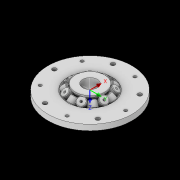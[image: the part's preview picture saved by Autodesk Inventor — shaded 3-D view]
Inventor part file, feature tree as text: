
AUTODESK INVENTOR PART (.ipt)
format: ipt  version: 2022.2 (Build 262287010, 287A)  size: 992,256 bytes
history: native  units: mm
features: other x35, extrude x26, sketch x16, pattern_circular x10, plane x4, fillet x2, move_body x2, revolve x2, draft x2, chamfer x2
ambient origin geometry x8: Origin, YZ Plane, XZ Plane, XY Plane, X Axis, Y Axis, Z Axis, Center Point
bodies: Solid5 (feature_tree)
feature tree (101):
  other  "CrossSection1"
  sketch  "Sketch7"  dims[d167=8.972256mm]
  other  "Roller1"
  other  "Roller2"
  sketch  "Sketch22"  dims[d173=10.814812mm d201=40.0mm]
  sketch  "Sketch2"  dims[d57=4.025mm d90=18.336628mm]
  sketch  "Sketch23"  dims[d232=0.0mm d233=3600.0mm d343=17.202946mm d344=17.117234mm]
  other  "RevRoller1"
  fillet  "Fillet1"  Radius=15.781563mm
  extrude  "Extrusion39"  Depth=18.336628mm
  pattern_circular  "Circular Pattern13"  Count=4  [1 undecoded]
  move_body  "Move Body7"
  revolve  "Revolution13"  [1 undecoded]
  fillet  "Fillet3"  Radius=17.117234mm
  pattern_circular  "Circular Pattern14"  [2 undecoded]
  move_body  "Move Body6"
  revolve  "Revolution14"  [1 undecoded]
  other  "OuterRim_Top2"
  other  "OuterRim_Bottom2"
  plane  "Work Plane8"
  sketch  "Sketch49"  dims[d352=0.025mm]
  sketch  "Sketch50"  dims[d354=0.025mm]
  sketch  "Sketch51"  dims[d355=17.202946mm]
  extrude  "Extrusion40"  TaperAngle=360.0deg  [1 undecoded]
  extrude  "Extrusion41"  Depth=0.5mm
  extrude  "Extrusion42"  Depth=0.5mm
  extrude  "Extrusion43"  Depth=0.5mm
  sketch  "Sketch52"  dims[d356=17.117234mm]
  extrude  "Extrusion44"  Depth=0.5mm
  extrude  "Extrusion45"  Depth=0.5mm
  extrude  "Extrusion46"  TaperAngle=90.0deg  [1 undecoded]
  extrude  "Extrusion47"  Depth=0.5mm
  pattern_circular  "Circular Pattern32"  Count=7  [1 undecoded]
  pattern_circular  "Circular Pattern33"  Angle=360.0deg  [1 undecoded]
  sketch  "Sketch57"  dims[d358=360.0deg d359=0.5mm d360=70.0mm d361=360.0deg d363=4.48799mm d367=8.1mm d370=0.025mm d371=1.0mm d372=4.48799mm d373=90.0deg d374=0.5mm d375=70.0mm d376=360.0deg d378=90.0deg d379=0.1mm d380=0.025mm d381=0.025mm d382=0.025mm d383=0.025mm d384=10.620203mm d385=0.0mm d386=0.0mm d391=7.0mm d392=40.0mm d393=1.5mm d394=1.5mm d395=1.5mm d396=1.5mm d397=90.0deg d398=90.0deg d399=90.0deg d400=40.0mm d401=10.620203mm d402=0.0mm d486=0.436332mm d487=0.5mm d488=2.0mm d489=0.0mm d490=20.0mm d495=2.5mm d496=8.0mm d506=13.856406mm d507=55.5mm d508=8.0mm d509=0.05mm d510=2.5mm d511=30.0deg d512=12.0mm d513=6.0mm d514=0.2mm d515=30.0deg d516=131.0mm d517=65.5mm d518=0.2mm d519=100.0mm d520=120.0mm d521=2.0mm d522=150.0mm d530=50.0mm d531=5.5mm d532=5.5mm d533=5.5mm d534=85.75mm d535=73.5mm d536=61.25mm d537=24.5mm d538=3.0mm d539=2.4mm d540=0.0mm d541=0.0mm d542=0.0mm d543=5.5mm d544=3.0mm d545=0.0mm d546=90.0mm d547=360.0deg d549=3.0mm d550=3.0mm d551=2.4mm d552=0.0mm d553=5.310101mm d554=0.0mm d555=2.4mm d556=0.0mm d557=5.310101mm d558=0.0mm d559=5.310101mm d560=0.0mm d561=90.0mm d562=360.0deg d564=60.0mm d565=360.0deg d567=5.5mm d568=5.5mm d569=3.0mm d570=0.0mm d571=5.310101mm d572=0.0mm d573=3.0mm d574=0.0mm d575=5.310101mm d576=0.0mm d577=90.0mm d578=360.0deg d580=60.0mm d581=360.0deg d584=20.0mm d585=8.0mm d587=1.75mm d589=3.0mm d592=2.0mm d593=12.0mm d594=12.0mm d600=0.5mm d601=2.0mm d602=45.0deg d603=0.5mm d604=2.0mm d605=45.0deg d606=0.436332mm d607=0.5mm d608=0.0mm d609=20.0mm d611=360.0deg d613=0.0mm d614=0.0mm d617=0.99971mm d618=100.0mm d620=34.0mm d621=5.0mm d622=0.5mm d623=0.5mm d624=5.0mm d625=0.2mm d626=0.0mm d627=20.0mm d629=34.0mm d630=48.5mm d631=20.0mm d633=6.283185mm d635=5.5mm d636=3.0mm d637=7.0mm d638=4.0mm d639=5.310101mm d640=0.0mm d641=3.0mm d642=0.0mm d643=5.310101mm d644=0.0mm d645=4.0mm d646=0.0mm d647=20.0mm d649=6.283185mm d651=3.0mm d652=4.0mm d653=20.0mm d655=6.283185mm d657=7.0mm d658=5.5mm d659=5.310101mm d660=0.0mm d661=2.020203mm d662=0.0mm d663=5.310101mm d664=0.0mm d665=2.620203mm d666=0.0mm d679=50.0mm d680=360.0deg d682=50.0mm d683=360.0deg d694=6.35mm d695=6.35mm d696=6.4mm d697=5.45mm d698=11.194mm d699=0.0mm d700=8.194mm d701=0.0mm d702=60.0mm d703=360.0deg d705=0.0mm d706=0.0mm d707=0.0mm d708=0.0mm d709=0.0mm d710=0.0mm d711=0.0mm d712=0.0mm d713=0.0mm d714=0.0mm d715=0.0mm d716=0.0mm d16=0.872665mm d17=0.872665mm d49=0.872665mm d50=0.872665mm d51=0.872665mm d52=0.872665mm d236=0.5mm d237=0.872665mm d238=0.5mm d239=0.872665mm d282=1.0mm d283=1.0mm d284=1.0mm d285=0.15mm d286=0.25mm d287=0.375mm d288=14.3117mm d289=0.75mm d290=20.594885mm d291=0.0625mm d292=0.75mm d293=0.375mm d405=0.5mm d406=0.872665mm d407=0.5mm d408=0.872665mm d413=0.5mm d414=0.872665mm d415=0.5mm d416=0.872665mm d417=0.5mm d418=0.872665mm d419=0.5mm d420=0.872665mm d421=0.872665mm d431=0.5mm d432=0.872665mm d433=0.5mm d434=0.872665mm d471=0.5mm d472=0.872665mm d473=0.5mm d474=0.872665mm d497=0.5mm d498=0.872665mm d499=0.5mm d500=0.872665mm d590=0.5mm d591=0.872665mm]
  other  "UCS2"
  extrude  "Extrusion50"  TaperAngle=90.0deg  [1 undecoded]
  extrude  "Extrusion51"  Depth=0.1mm
  pattern_circular  "Circular Pattern34"  [2 undecoded]
  other  "UCS1"
  plane  "Work Plane7"
  sketch  "Sketch47"  dims[d350=17.202946mm]
  extrude  "Rotor_Ring"  Depth=0.5mm
  draft  "FaceDraft2"
  sketch  "Sketch30"  dims[d345=0.025mm]
  plane  "Work Plane5"
  other  "Rotor Featurs"
  other  "RotorRim_Bottom"
  extrude  "Extrusion24"  Depth=0.5mm
  extrude  "Extrusion25"  Depth=0.5mm
  extrude  "Extrusion26"  Depth=10.620203mm
  pattern_circular  "Circular Pattern23"  [2 undecoded]
  sketch  "Sketch41"  dims[d347=0.1mm]
  extrude  "Extrusion27"  TaperAngle=0.0deg  [1 undecoded]
  extrude  "Extrusion28"  Depth=7.0mm
  pattern_circular  "Circular Pattern24"  Count=4  [1 undecoded]
  extrude  "Extrusion29"  Depth=0.5mm
  extrude  "Extrusion30"  Depth=0.5mm
  extrude  "Extrusion31"  Depth=0.5mm
  pattern_circular  "Circular Pattern25"  [2 undecoded]
  sketch  "Sketch42"  dims[d348=0.1mm]
  extrude  "Extrusion32"  TaperAngle=90.0deg  [1 undecoded]
  extrude  "Extrusion33"  TaperAngle=90.0deg  [1 undecoded]
  extrude  "Extrusion34"  TaperAngle=90.0deg  [1 undecoded]
  extrude  "Extrusion35"  Depth=40.0mm
  pattern_circular  "Circular Pattern26"  [2 undecoded]
  pattern_circular  "Circular Pattern27"  [2 undecoded]
  chamfer  "Chamfer1"  Distance=0.436332mm
  chamfer  "Chamfer2"  Distance=0.5mm
  draft  "FaceDraft4"
  plane  "Work Plane6"
  sketch  "Sketch43"  dims[d349=17.117234mm]
  extrude  "Extrusion37"  Depth=0.5mm
  extrude  "Extrusion38"  Depth=8.0mm
  other  "2D Equation Curve1"
  sketch  "Sketch40"  dims[d346=0.025mm]
  other  "Work Axis6"
  other  "Work Axis7"
  other  "Work Axis8"
  other  "Work Axis9"
  other  "Work Axis10"
  other  "Work Point1"
  other  "Work Point2"
  other  "Work Point3"
  other  "Work Point4"
  other  "Work Point5"
  sketch  "Sketch48"  dims[d351=0.025mm]
  other  "UCS1: YZ Plane"
  other  "UCS1: XZ Plane"
  other  "UCS1: XY Plane"
  other  "UCS1: X Axis"
  other  "UCS1: Y Axis"
  other  "UCS1: Z Axis"
  other  "UCS1: Center Point"
  other  "UCS2: YZ Plane"
  other  "UCS2: XZ Plane"
  other  "UCS2: XY Plane"
  other  "UCS2: X Axis"
  other  "UCS2: Y Axis"
  other  "UCS2: Z Axis"
  other  "UCS2: Center Point"
note: 25 required parameter values undecoded (feature->parameter linkage not recoverable at this tier; creation-order binding heuristic only, values carry confidence <= 0.55)